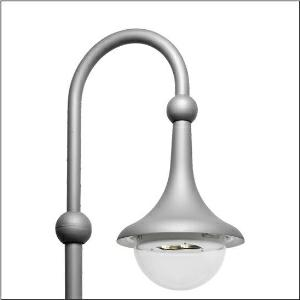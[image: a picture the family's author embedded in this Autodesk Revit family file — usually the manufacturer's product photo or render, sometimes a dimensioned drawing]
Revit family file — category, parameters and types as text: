
# Revit family: grosse_glocke_iq___st1_2a_5xa1565e1f108_d4d8
name_source: partatom
category: Lighting Fixtures
units: mm (PartAtom-declared; Revit-internal decimal feet)

## family parameters
Cut with Voids When Loaded = No
Host = Face
Light Source = No
Part Type = Normal
Room Calculation Point = No
Round Connector Dimension = Use Diameter
Shared = No

## types (1)
- --- (1 x LED, 5180 lm, 34.3 W, 3000K)
    Apparent Load = 34 VA
    CIE Flux Codes = 28 66 95 100 100
    Color Rendering = 70
    Color Temperature = 3000K
    Default Elevation = 1800 mm
    Description = Large Bell iQ, mast luminaire, primary light control with 3 zone facetted reflector, of plastic, silver coated, primary optical cover: enclosure, of PMMA, transparent, light distribution: ST1.2a, light emission: direct distribution, primary light characteristic: asymmetric, installation type: suspended mounting, High Power LED, rated luminous flux: 5.180lm, luminous efficacy: 151lm/W, light colour: 730, colour temperature: 3000K, control gear: iQ Street-Remote, control: optimised constant luminous flux control (CLO 2.0), Desk-Remote (wireless, voltage-free reading and setting of iQ features in the workshop via application-optimized NFC function/RFID function), Light-Fading, Smart-Wire, Night-Set, Lumen-Switch, Temp-Guard, Auto-Match, Street-Remote, pre-setting: logarithmic dimming characteristic, mains connection: 230..240V, AC, 50/60Hz, start of lifetime: 34W, end of service life: 38W, reduction: 16W, luminaire housing, bell-shaped, of glass-fibre reinforced polyester, coated, Siteco® metallic grey (DB 702S), please order curved mast extension separately, diameter: 530mm, height: 695mm, mounting height: 4..6m, protection rating (complete): IP54, insulation class (complete): insulation class II (safety insulation), certification: CE, ENEC, VDE, impact resistance: IK08, standard-compliant lighting for roads and squares, packaging unit: 1 piece

Light Distribution: ST1.2a
    Height = 695 mm
    Lamp = 1 x LED
    Lamp Light Flux = 5180 lm
    Lamp Power = 34.3 W
    Lamp count = 1
    Length = 530 mm
    Luminous efficacy = 151 lm/W
    Manufacturer = Siteco
    ModVariant = No
    Model = 5XA1565E1F108
    Mounting Place = Pole
    Mounting Type = Pole annexe
    Number of Poles = 1
    OnlyDefault = Yes
    Power Factor = 1
    Product Name = Große Glocke iQ | ST1.2a
    Product group = mast luminaire | pylon annexe
    ProductGroupID = 6200
    Protection Class = Protection class II
    Protection Degree = IP 54
    RLX_Detail_Level = 1
    RLX_Emergency_Light_Flux = 0 lm
    RLX_Emergency_Type = 0
    RLX_Emergency_Type_DB = No
    RlxData = <blob elided: 85369 chars, md5=7dc495bd>
    Socket = socket
    Standby Power = 0 W
    System Light Flux = 5180 lm
    System Power = 34 W
    Type Comments = factory setting: luminous flux: 100 % | dim-lin: 254 | 640 mA
    Type Image = l_1347688.jpg
    URL = http://relux.com
    VarID = @adj_067799
    Voltage = 0 V
    Weight = 0.00 kg
    Width = 0 mm  [stored 0 ft]

note: [stored X ft] marks values corroborated as IEEE doubles in the binary element streams (Revit-internal decimal feet)

## geometry (parser evidence)
native form markers: Blend x4, Sweep x11
no freeform markers — native parametric forms only
